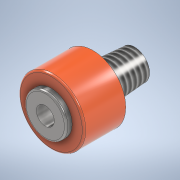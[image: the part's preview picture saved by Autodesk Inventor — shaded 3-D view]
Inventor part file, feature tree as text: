
AUTODESK INVENTOR PART (.ipt)
format: ipt  version: 2020 (Build 240168000, 168)  size: 163,328 bytes
history: native  units: mm
features: sketch x6, extrude x2, hole x2, fillet x2, plane x1, loft x1, thread x1
ambient origin geometry x8: Origin, YZ Plane, XZ Plane, XY Plane, X Axis, Y Axis, Z Axis, Center Point
bodies: Solid1 (feature_tree)
feature tree (15):
  extrude  "Extrusion1"  Depth=7.0mm TaperAngle=0.0deg
  extrude  "Extrusion2"  Depth=1.0mm TaperAngle=0.0deg
  hole  "Hole1"  [1 undecoded]
  fillet  "Fillet1"  Radius=0.3mm
  fillet  "Fillet2"  Radius=6.0mm
  sketch  "Sketch5"  dims[d8=3.0mm d9=6.0mm d10=4.0mm d11=2.0mm d12=90.0deg d13=8.0mm d14=20.594885mm d15=0.3mm d16=0.3mm d17=6.0mm]
  plane  "Work Plane1"
  loft  "Loft1"
  hole  "Hole2"  [1 undecoded]
  thread  "Thread1"  [1 undecoded]
  sketch  "Sketch1"  dims[d0=11.0mm d1=7.0mm d2=0.0mm]
  sketch  "Sketch2"  dims[d3=7.0mm d4=1.0mm d5=0.0mm]
  sketch  "Sketch4"  dims[d7=3.0mm]
  sketch  "Sketch6"  dims[d18=7.0mm d19=5.0mm]
  sketch  "Sketch7"  dims[d20=0.0mm d21=90.0deg d22=0.0mm d23=90.0deg d24=3.0mm d25=6.0mm d26=4.0mm d27=2.0mm d28=90.0deg d29=8.0mm d30=20.594885mm d31=9.0mm d32=0.0mm]
note: 3 required parameter values undecoded (feature->parameter linkage not recoverable at this tier; creation-order binding heuristic only, values carry confidence <= 0.55)
